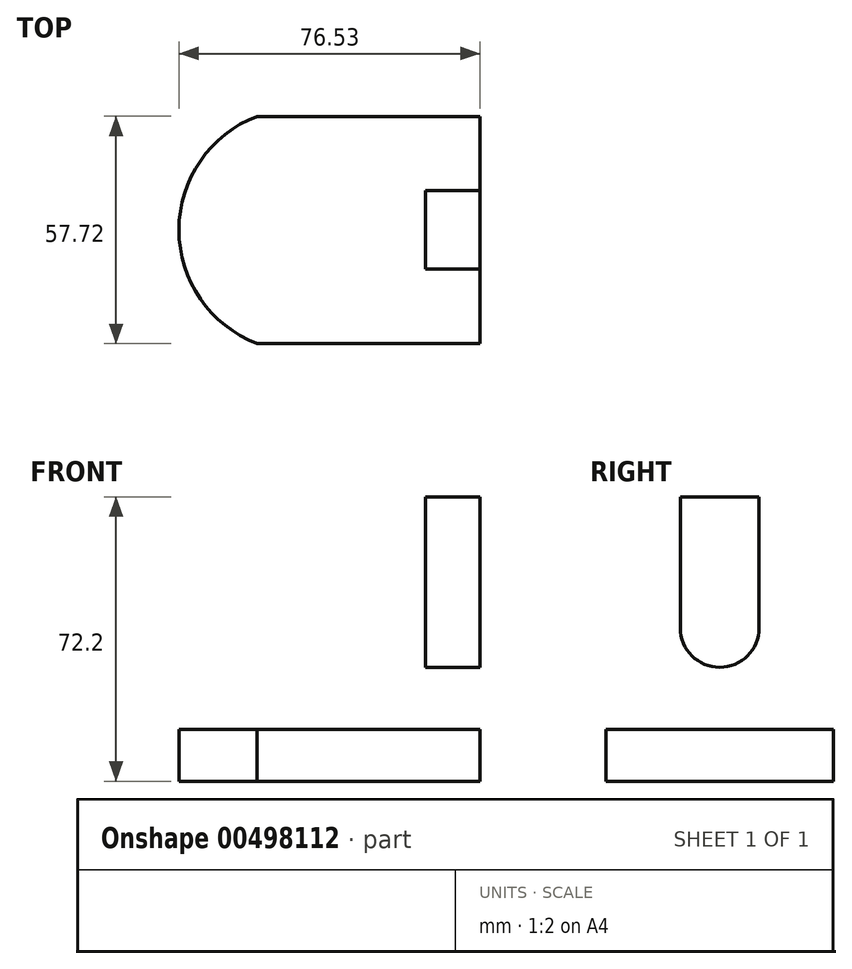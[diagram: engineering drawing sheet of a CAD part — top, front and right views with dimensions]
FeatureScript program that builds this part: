
annotation { "Feature Type Name" : "Feature", "Feature Type Description" : "" }
export const myFeature = defineFeature(function(context is Context, id is Id, definition is map)
    precondition{}
    {
        {
            var Q0;
            Q0=qCreatedBy(makeId("Top.planeOp"),FACE);
            var sketch = newSketch(context, id + "F0", { "sketchPlane" : qUnion([Q0])});
            skLineSegment(sketch, "E0.bottom", {"start": v(28.34, -28.86) * mm, "end": v(-28.34, -28.86) * mm});
            skLineSegment(sketch, "E0.top", {"start": v(28.34, 28.86) * mm, "end": v(-28.34, 28.86) * mm});
            skLineSegment(sketch, "E0.left", {"start": v(28.34, -28.86) * mm, "end": v(28.34, 28.86) * mm});
            skPoint(sketch, "E0.middle", {"position": v(0, 0) * mm});
            skArc(sketch, "E1", {"start": v(-28.34, 28.86) * mm, "mid": v(-48.19, 0) * mm, "end": v(-28.34, -28.86) * mm});
            skLineSegment(sketch, "E2", {"start": v(14.5, 28.86) * mm, "end": v(14.5, -28.86) * mm});
            skSolve(sketch);
        }
        {
            var Q0;
            Q0 = qSketchRegion(id + "F0", true);
            extrude(context, id + "F1", {"entities" : qUnion([Q0]), "depth" : 13.1 * mm});
        }
        {
            var Q0;
            {var subQ0=sQuery(id+"F0.wireOp",EDGE,"E0.left");Q0=makeQuery(id+"F0.imprint","IMPRINT",FACE,{"disambiguationData":[TD([[makeQuery(id+"F0.imprint","IMPRINT",EDGE,{"derivedFrom":subQ0}),1.0]])]});}
            extrude(context, id + "F2", {"entities" : qUnion([Q0]), "operationType" : NewBodyOperationType.ADD, "depth" : 72.2 * mm});
        }
        {
            var Q0;
            Q0=makeQuery(id+"F2.opExtrude","SWEPT_FACE",FACE,{"disambiguationData":[OSD([sQuery(id+"F0.wireOp",EDGE,"E2")])]});
            var sketch = newSketch(context, id + "F3", { "sketchPlane" : qUnion([Q0])});
            skLineSegment(sketch, "E3", {"start": v(0, 72.2) * mm, "end": v(0, 38.93) * mm, "construction": true});
            skPoint(sketch, "E3.endSnap0", {"position": v(0, 72.2) * mm});
            skArc(sketch, "E4.0.startCap", {"start": v(-10, 72.2) * mm, "mid": v(0, 82.2) * mm, "end": v(10, 72.2) * mm});
            skArc(sketch, "E4.0.endCap", {"start": v(10, 38.93) * mm, "mid": v(0, 28.93) * mm, "end": v(-10, 38.93) * mm});
            skLineSegment(sketch, "E4.0.left", {"start": v(10, 72.2) * mm, "end": v(10, 38.93) * mm});
            skLineSegment(sketch, "E4.0.right", {"start": v(-10, 72.2) * mm, "end": v(-10, 38.93) * mm});
            skSolve(sketch);
        }
        {
            var Q0;
            Q0=makeQuery(id+"F3.imprint","IMPRINT",FACE,{"disambiguationData":[TD([[makeQuery(id+"F3.imprint","IMPRINT",EDGE,{"derivedFrom":sQuery(id+"F3.wireOp",EDGE,"E4.0.endCap")}),-1.0]])]});
            var Q1;
            {var subQ0=sQuery(id+"F3.wireOp",EDGE,"E4.0.startCap");Q1=makeQuery(id+"F3.imprint","IMPRINT",FACE,{"disambiguationData":[TD([[makeQuery(id+"F3.imprint","IMPRINT",EDGE,{"derivedFrom":subQ0}),-1.0]])]});}
            extrude(context, id + "F4", {"entities" : qUnion([Q0, Q1]), "operationType" : NewBodyOperationType.REMOVE, "endBound" : BoundingType.THROUGH_ALL, "oppositeDirection" : true, "depth" : 25 * mm});
        }
        {
            var Q0;
            {var subQ0=sQuery(id+"F0.wireOp",EDGE,"E0.bottom");Q0=makeQuery(id+"F2.boolean.opBoolean","MERGE",FACE,{"derivedFrom":[makeQuery(id+"F1.opExtrude","SWEPT_FACE",FACE,{"disambiguationData":[OSD([subQ0])]}),makeQuery(id+"F2.opExtrude","SWEPT_FACE",FACE,{"disambiguationData":[OSD([subQ0])]})]});}
            var sketch = newSketch(context, id + "F5", { "sketchPlane" : qUnion([Q0])});
            skLineSegment(sketch, "E5.bottom", {"start": v(4.45, 23.29) * mm, "end": v(52.23, 23.29) * mm});
            skLineSegment(sketch, "E5.top", {"start": v(4.45, -23.29) * mm, "end": v(52.23, -23.29) * mm});
            skLineSegment(sketch, "E5.left", {"start": v(4.45, 23.29) * mm, "end": v(4.45, -23.29) * mm});
            skLineSegment(sketch, "E5.right", {"start": v(52.23, 23.29) * mm, "end": v(52.23, -23.29) * mm});
            skPoint(sketch, "E5.middle", {"position": v(28.34, 0) * mm});
            skSolve(sketch);
        }
        {
            var Q0;
            {var subQ0=sQuery(id+"F0.wireOp",EDGE,"E0.bottom");var subQ5=sQuery(id+"F5.wireOp",EDGE,"E5.left");var subQ7=makeQuery(id+"F1.opExtrude","CAP_EDGE",EDGE,{"disambiguationData":[OSD([subQ0])],"isStart":false});var subQ8=makeQuery(id+"F5.imprint","INTERSECT",VERTEX,{"derivedFrom":[subQ7,subQ5]});Q0=makeQuery(id+"F5.imprint","IMPRINT",FACE,{"disambiguationData":[TD([[makeQuery(id+"F5.imprint","IMPRINT",EDGE,{"disambiguationData":[TD([[subQ8,-1.0]])],"derivedFrom":subQ5}),1.0]])]});}
            extrude(context, id + "F6", {"entities" : qUnion([Q0]), "operationType" : NewBodyOperationType.REMOVE, "oppositeDirection" : true, "depth" : 13.5 * mm});
        }
    });
